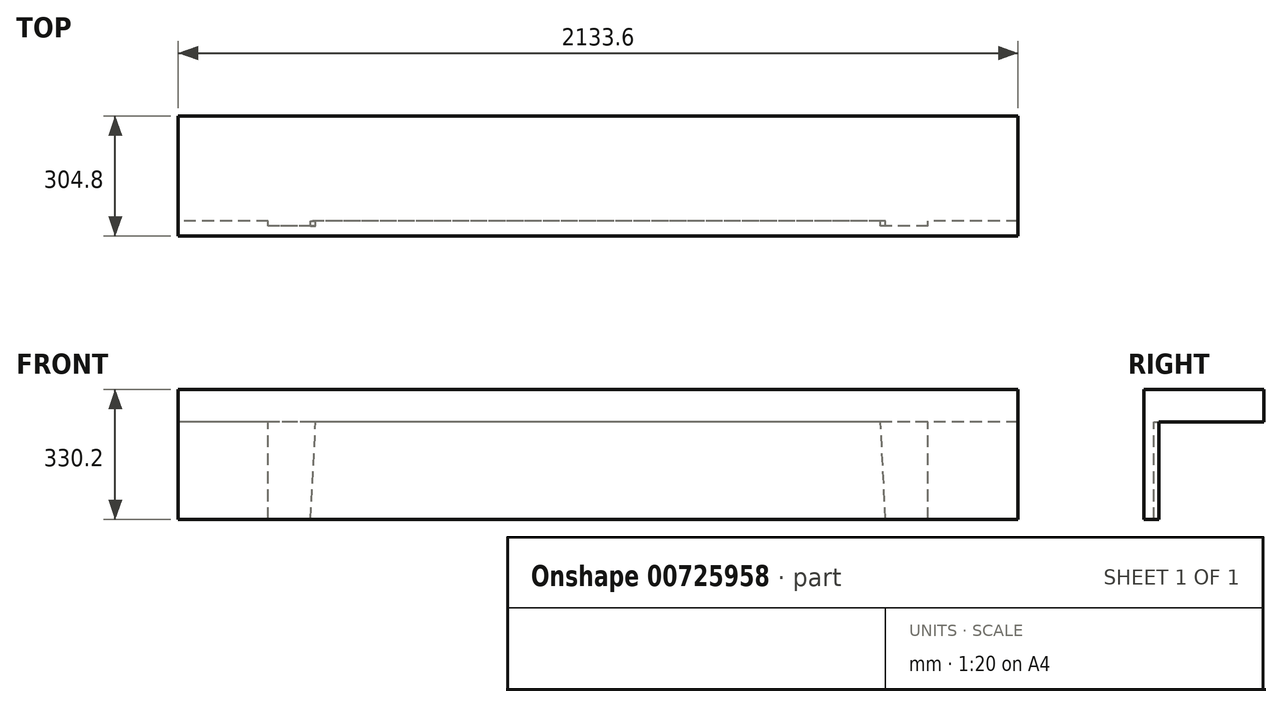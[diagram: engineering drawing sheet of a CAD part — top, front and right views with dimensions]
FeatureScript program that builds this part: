
annotation { "Feature Type Name" : "Feature", "Feature Type Description" : "" }
export const myFeature = defineFeature(function(context is Context, id is Id, definition is map)
    precondition{}
    {
        {
            var Q0;
            Q0=qCreatedBy(makeId("Right.planeOp"),FACE);
            var sketch = newSketch(context, id + "F0", { "sketchPlane" : qUnion([Q0])});
            skLineSegment(sketch, "E0", {"start": v(0, 0) * mm, "end": v(0, -330.2) * mm});
            skLineSegment(sketch, "E1", {"start": v(0, -330.2) * mm, "end": v(38.1, -330.2) * mm});
            skLineSegment(sketch, "E2", {"start": v(38.1, -330.2) * mm, "end": v(38.1, -82.55) * mm});
            skLineSegment(sketch, "E3", {"start": v(38.1, -82.55) * mm, "end": v(304.8, -82.55) * mm});
            skLineSegment(sketch, "E4", {"start": v(304.8, -82.55) * mm, "end": v(304.8, 0) * mm});
            skLineSegment(sketch, "E5", {"start": v(304.8, 0) * mm, "end": v(0, 0) * mm});
            skSolve(sketch);
        }
        {
            var Q0;
            Q0 = qSketchRegion(id + "F0", true);
            extrude(context, id + "F1", {"entities" : qUnion([Q0]), "flatOperationType" : FlatOperationType.REMOVE, "depth" : 2133.6 * mm, "offsetDistance" : 25.4 * mm, "domain" : OperationDomain.MODEL});
        }
        {
            var Q0;
            Q0=makeQuery(id+"F1.opExtrude","SWEPT_FACE",FACE,{"disambiguationData":[OSD([sQuery(id+"F0.wireOp",EDGE,"E2")])]});
            var sketch = newSketch(context, id + "F2", { "sketchPlane" : qUnion([Q0])});
            skLineSegment(sketch, "E6", {"start": v(-1066.8, -330.2) * mm, "end": v(-1066.8, -82.55) * mm, "construction": true});
            skLineSegment(sketch, "E7.bottom", {"start": v(-1905, -330.2) * mm, "end": v(-1822.45, -330.2) * mm});
            skLineSegment(sketch, "E7.top", {"start": v(-1905, -82.55) * mm, "end": v(-1822.45, -82.55) * mm});
            skLineSegment(sketch, "E7.left", {"start": v(-1905, -330.2) * mm, "end": v(-1905, -82.55) * mm});
            skLineSegment(sketch, "E7.right", {"start": v(-1822.45, -330.2) * mm, "end": v(-1822.45, -82.55) * mm, "construction": true});
            skLineSegment(sketch, "E8", {"start": v(-1822.45, -330.2) * mm, "end": v(-1797.05, -330.2) * mm});
            skLineSegment(sketch, "E9", {"start": v(-1797.05, -330.2) * mm, "end": v(-1784.35, -82.55) * mm});
            skLineSegment(sketch, "E10", {"start": v(-1784.35, -82.55) * mm, "end": v(-1822.45, -82.55) * mm});
            skLineSegment(sketch, "E11.MirrorCS", {"start": v(-349.25, -82.55) * mm, "end": v(-311.15, -82.55) * mm});
            skLineSegment(sketch, "E12.MirrorCS", {"start": v(-311.15, -330.2) * mm, "end": v(-336.55, -330.2) * mm});
            skLineSegment(sketch, "E13.MirrorCS", {"start": v(-228.6, -82.55) * mm, "end": v(-311.15, -82.55) * mm});
            skLineSegment(sketch, "E14.MirrorCS", {"start": v(-228.6, -330.2) * mm, "end": v(-228.6, -82.55) * mm});
            skLineSegment(sketch, "E15.MirrorCS", {"start": v(-311.15, -330.2) * mm, "end": v(-311.15, -82.55) * mm, "construction": true});
            skLineSegment(sketch, "E16.MirrorCS", {"start": v(-228.6, -330.2) * mm, "end": v(-311.15, -330.2) * mm});
            skLineSegment(sketch, "E17.MirrorCS", {"start": v(-336.55, -330.2) * mm, "end": v(-349.25, -82.55) * mm});
            skSolve(sketch);
        }
        {
            var Q0;
            Q0 = qSketchRegion(id + "F2", true);
            extrude(context, id + "F3", {"entities" : qUnion([Q0]), "operationType" : NewBodyOperationType.REMOVE, "oppositeDirection" : true, "depth" : 12.7 * mm, "offsetDistance" : 25.4 * mm});
        }
    });
